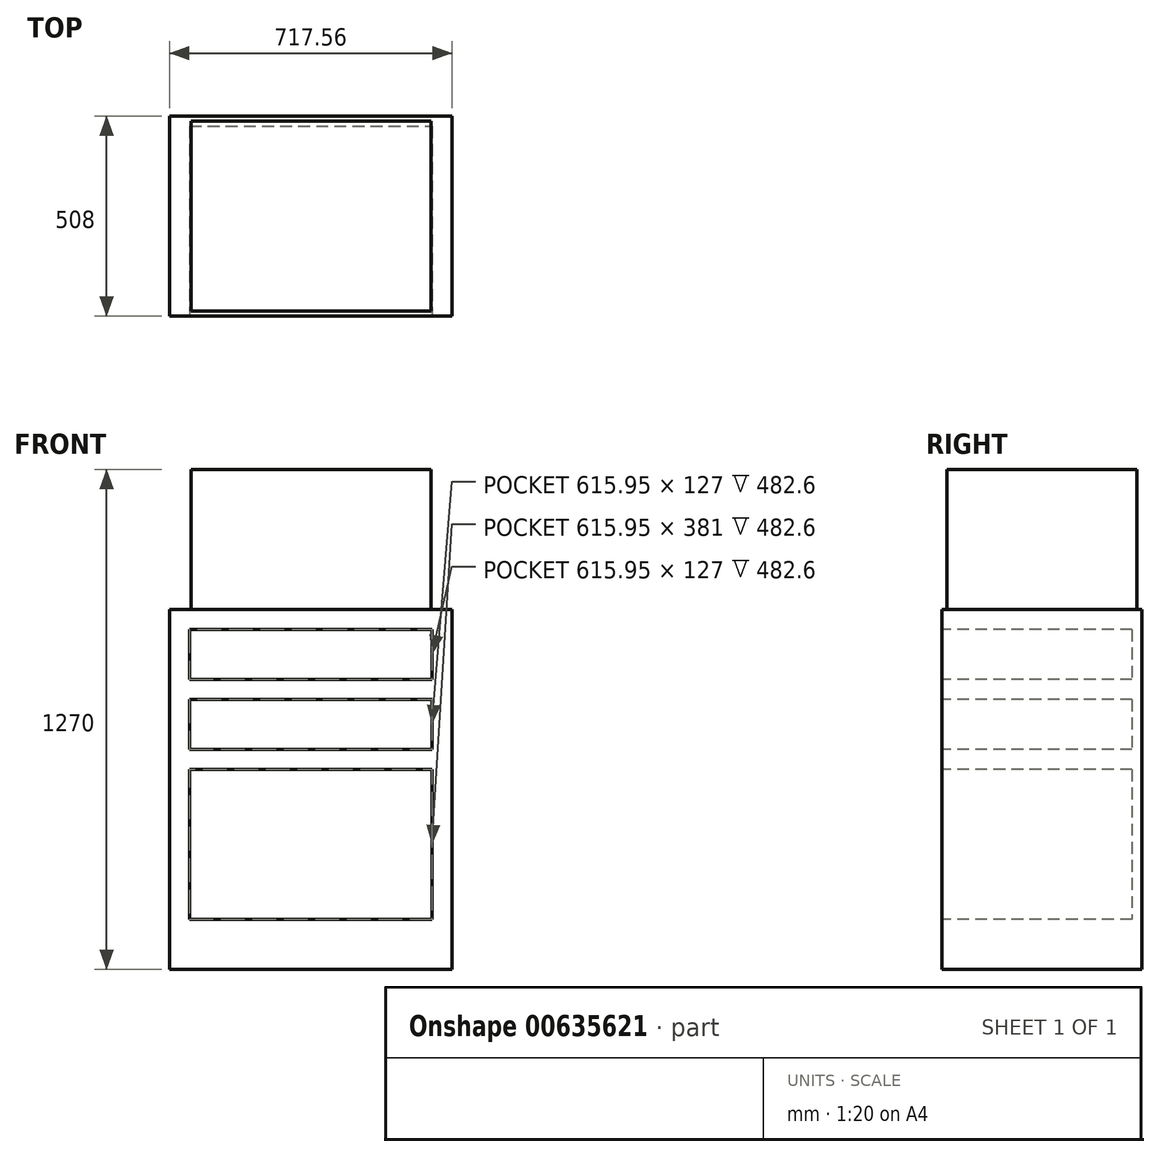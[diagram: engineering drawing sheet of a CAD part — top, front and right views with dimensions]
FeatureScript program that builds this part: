
annotation { "Feature Type Name" : "Feature", "Feature Type Description" : "" }
export const myFeature = defineFeature(function(context is Context, id is Id, definition is map)
    precondition{}
    {
        {
            var Q0;
            Q0=qCreatedBy(makeId("Top.planeOp"),FACE);
            var sketch = newSketch(context, id + "F0", { "sketchPlane" : qUnion([Q0])});
            skLineSegment(sketch, "E0.bottom", {"start": v(-358.78, -254) * mm, "end": v(358.78, -254) * mm});
            skLineSegment(sketch, "E0.top", {"start": v(-358.78, 254) * mm, "end": v(358.78, 254) * mm});
            skLineSegment(sketch, "E0.left", {"start": v(-358.78, -254) * mm, "end": v(-358.78, 254) * mm});
            skLineSegment(sketch, "E0.right", {"start": v(358.78, -254) * mm, "end": v(358.78, 254) * mm});
            skPoint(sketch, "E0.middle", {"position": v(0, 0) * mm});
            skSolve(sketch);
        }
        {
            var Q0;
            Q0 = qSketchRegion(id + "F0", true);
            extrude(context, id + "F1", {"entities" : qUnion([Q0]), "depth" : 914.4 * mm, "offsetDistance" : 25.4 * mm});
        }
        {
            var Q0;
            Q0=makeQuery(id+"F1.opExtrude","CAP_FACE",FACE,{"disambiguationData":[OSD([sQuery(id+"F0.wireOp",EDGE,"E0.bottom"),sQuery(id+"F0.wireOp",EDGE,"E0.top"),sQuery(id+"F0.wireOp",EDGE,"E0.left"),sQuery(id+"F0.wireOp",EDGE,"E0.right")])],"isStart":false});
            var sketch = newSketch(context, id + "F2", { "sketchPlane" : qUnion([Q0])});
            skLineSegment(sketch, "E1.bottom", {"start": v(304.8, -241.3) * mm, "end": v(-304.8, -241.3) * mm});
            skLineSegment(sketch, "E1.top", {"start": v(304.8, 241.3) * mm, "end": v(-304.8, 241.3) * mm});
            skLineSegment(sketch, "E1.left", {"start": v(304.8, -241.3) * mm, "end": v(304.8, 241.3) * mm});
            skLineSegment(sketch, "E1.right", {"start": v(-304.8, -241.3) * mm, "end": v(-304.8, 241.3) * mm});
            skPoint(sketch, "E1.middle", {"position": v(0, 0) * mm});
            skSolve(sketch);
        }
        {
            var Q0;
            Q0 = qSketchRegion(id + "F2", true);
            extrude(context, id + "F3", {"entities" : qUnion([Q0]), "depth" : 355.6 * mm, "offsetDistance" : 25.4 * mm});
        }
        {
            var Q0;
            Q0=makeQuery(id+"F1.opExtrude","SWEPT_FACE",FACE,{"disambiguationData":[OSD([sQuery(id+"F0.wireOp",EDGE,"E0.bottom")])]});
            var sketch = newSketch(context, id + "F4", { "sketchPlane" : qUnion([Q0])});
            skLineSegment(sketch, "E2.bottom", {"start": v(-307.98, 863.6) * mm, "end": v(307.98, 863.6) * mm});
            skLineSegment(sketch, "E2.top", {"start": v(-307.98, 736.6) * mm, "end": v(307.98, 736.6) * mm});
            skLineSegment(sketch, "E2.left", {"start": v(-307.98, 863.6) * mm, "end": v(-307.98, 736.6) * mm});
            skLineSegment(sketch, "E2.right", {"start": v(307.98, 863.6) * mm, "end": v(307.98, 736.6) * mm});
            skLineSegment(sketch, "E3.bottom", {"start": v(-307.98, 508) * mm, "end": v(307.98, 508) * mm});
            skLineSegment(sketch, "E3.top", {"start": v(-307.98, 127) * mm, "end": v(307.98, 127) * mm});
            skLineSegment(sketch, "E3.left", {"start": v(-307.98, 508) * mm, "end": v(-307.98, 127) * mm});
            skLineSegment(sketch, "E3.right", {"start": v(307.98, 508) * mm, "end": v(307.98, 127) * mm});
            skLineSegment(sketch, "E4.bottom", {"start": v(-307.98, 685.8) * mm, "end": v(307.98, 685.8) * mm});
            skLineSegment(sketch, "E4.top", {"start": v(-307.98, 558.8) * mm, "end": v(307.98, 558.8) * mm});
            skLineSegment(sketch, "E4.left", {"start": v(-307.98, 685.8) * mm, "end": v(-307.98, 558.8) * mm});
            skLineSegment(sketch, "E4.right", {"start": v(307.98, 685.8) * mm, "end": v(307.98, 558.8) * mm});
            skLineSegment(sketch, "E5.bottom", {"start": v(295.28, 850.9) * mm, "end": v(-295.28, 850.9) * mm, "construction": true});
            skLineSegment(sketch, "E5.top", {"start": v(295.28, 749.3) * mm, "end": v(-295.28, 749.3) * mm, "construction": true});
            skLineSegment(sketch, "E5.left", {"start": v(295.28, 850.9) * mm, "end": v(295.28, 749.3) * mm, "construction": true});
            skLineSegment(sketch, "E5.right", {"start": v(-295.28, 850.9) * mm, "end": v(-295.28, 749.3) * mm, "construction": true});
            skLineSegment(sketch, "E6.bottom", {"start": v(295.27, 673.1) * mm, "end": v(-295.28, 673.1) * mm, "construction": true});
            skLineSegment(sketch, "E6.top", {"start": v(295.27, 571.5) * mm, "end": v(-295.28, 571.5) * mm, "construction": true});
            skLineSegment(sketch, "E6.left", {"start": v(295.27, 673.1) * mm, "end": v(295.27, 571.5) * mm, "construction": true});
            skLineSegment(sketch, "E6.right", {"start": v(-295.28, 673.1) * mm, "end": v(-295.28, 571.5) * mm, "construction": true});
            skSolve(sketch);
        }
        {
            var Q0;
            Q0 = qSketchRegion(id + "F4", true);
            extrude(context, id + "F5", {"entities" : qUnion([Q0]), "operationType" : NewBodyOperationType.REMOVE, "oppositeDirection" : true, "depth" : 482.6 * mm, "offsetDistance" : 25.4 * mm});
        }
    });
